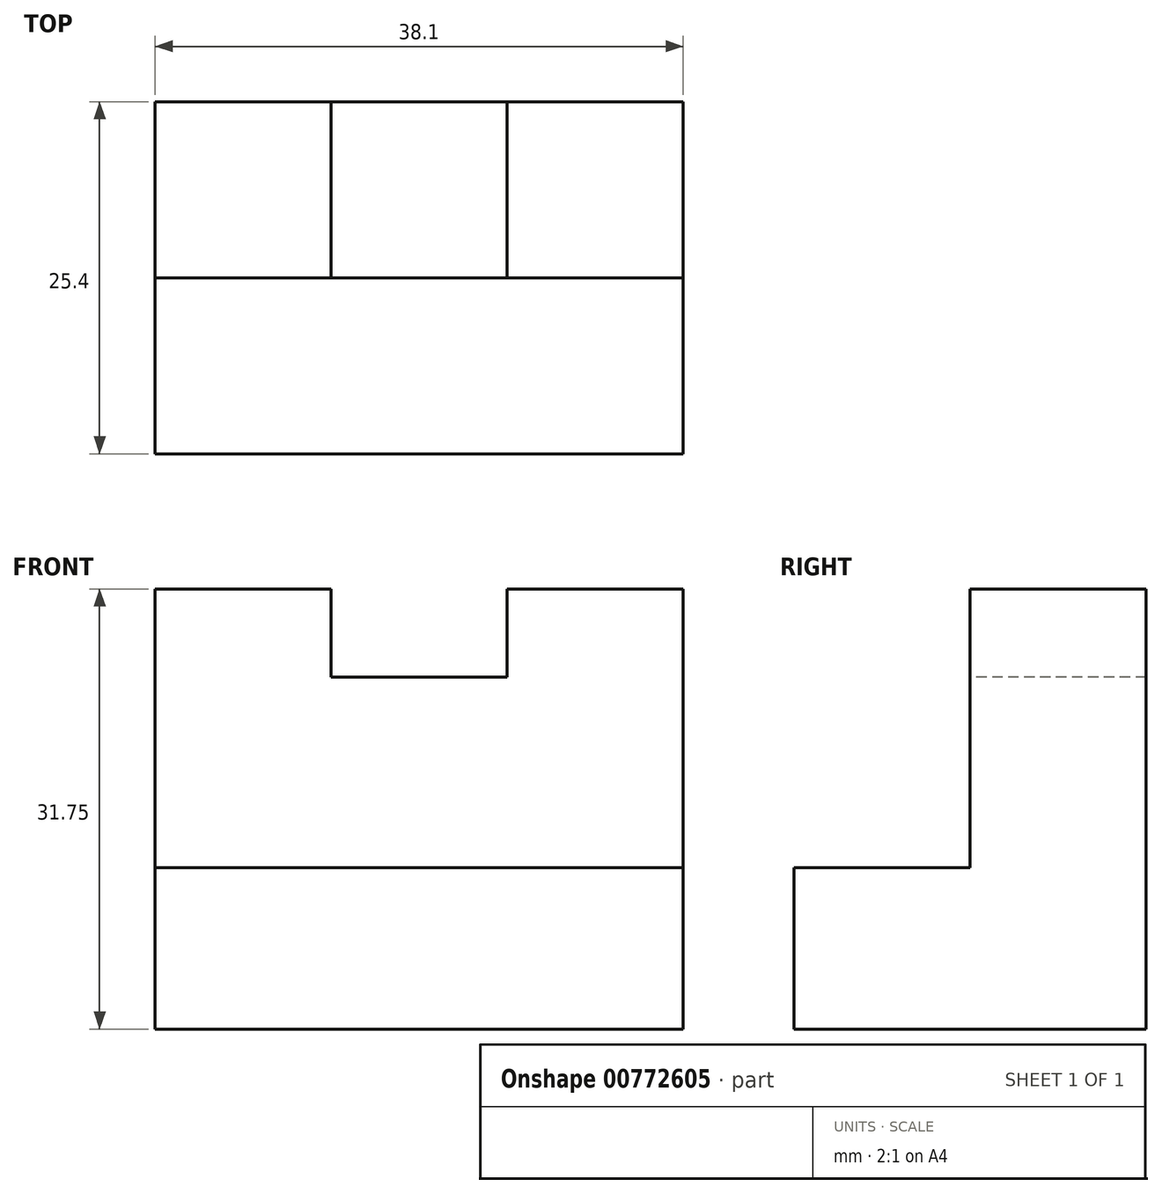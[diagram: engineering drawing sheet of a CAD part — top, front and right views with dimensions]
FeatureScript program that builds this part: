
annotation { "Feature Type Name" : "Feature", "Feature Type Description" : "" }
export const myFeature = defineFeature(function(context is Context, id is Id, definition is map)
    precondition{}
    {
        {
            var Q0;
            Q0=qCreatedBy(makeId("Right.planeOp"),FACE);
            var sketch = newSketch(context, id + "F0", { "sketchPlane" : qUnion([Q0])});
            skLineSegment(sketch, "E0", {"start": v(0, 0) * mm, "end": v(25.4, 0) * mm});
            skLineSegment(sketch, "E1", {"start": v(25.4, 0) * mm, "end": v(25.4, 31.75) * mm});
            skLineSegment(sketch, "E2", {"start": v(25.4, 31.75) * mm, "end": v(12.7, 31.75) * mm});
            skLineSegment(sketch, "E3", {"start": v(0, 0) * mm, "end": v(0, 11.63) * mm});
            skLineSegment(sketch, "E4", {"start": v(0, 11.63) * mm, "end": v(12.7, 11.63) * mm});
            skLineSegment(sketch, "E5", {"start": v(12.7, 31.75) * mm, "end": v(12.7, 11.63) * mm});
            skSolve(sketch);
        }
        {
            var Q0;
            Q0=makeQuery(id+"F0.imprint","IMPRINT",FACE,{"disambiguationData":[TD([[makeQuery(id+"F0.imprint","IMPRINT",EDGE,{"derivedFrom":sQuery(id+"F0.wireOp",EDGE,"E0")}),1.0]])]});
            extrude(context, id + "F1", {"entities" : qUnion([Q0]), "depth" : 38.1 * mm, "offsetDistance" : 25.4 * mm});
        }
        {
            var Q0;
            Q0=makeQuery(id+"F1.opExtrude","SWEPT_FACE",FACE,{"disambiguationData":[OSD([sQuery(id+"F0.wireOp",EDGE,"E5")])]});
            var sketch = newSketch(context, id + "F2", { "sketchPlane" : qUnion([Q0])});
            skLineSegment(sketch, "E6", {"start": v(0, 31.75) * mm, "end": v(12.7, 31.75) * mm});
            skLineSegment(sketch, "E7", {"start": v(12.7, 31.75) * mm, "end": v(12.7, 25.4) * mm});
            skLineSegment(sketch, "E8", {"start": v(12.7, 25.4) * mm, "end": v(25.4, 25.4) * mm});
            skLineSegment(sketch, "E9", {"start": v(25.4, 25.4) * mm, "end": v(25.4, 31.75) * mm});
            skSolve(sketch);
        }
        {
            var Q0;
            {var subQ0=sQuery(id+"F2.wireOp",EDGE,"E7");Q0=makeQuery(id+"F2.imprint","IMPRINT",FACE,{"disambiguationData":[TD([[makeQuery(id+"F2.imprint","IMPRINT",EDGE,{"derivedFrom":subQ0}),1.0]])]});}
            extrude(context, id + "F3", {"entities" : qUnion([Q0]), "operationType" : NewBodyOperationType.REMOVE, "oppositeDirection" : true, "depth" : 25.4 * mm, "offsetDistance" : 25.4 * mm});
        }
    });
